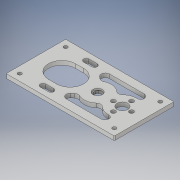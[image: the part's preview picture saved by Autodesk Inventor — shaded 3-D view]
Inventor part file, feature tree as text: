
AUTODESK INVENTOR PART (.ipt)
format: ipt  version: 2018 (Build 220112000, 112)  size: 195,584 bytes
history: native  units: in
note: dims shown in document units (in); Inventor stores cm internally (conversion verified against a paired STEP export)
features: extrude x1, sketch x1, fillet x1
ambient origin geometry x8: Origin, YZ Plane, XZ Plane, XY Plane, X Axis, Y Axis, Z Axis, Center Point
bodies: Solid1 (feature_tree)
feature tree (3):
  extrude  "Extrusion1"  Depth=0.1875in TaperAngle=0.0deg
  sketch  "Sketch1"  dims[d0=0.17in d1=0.1875in d2=0.0in]
  fillet  "Fillet3"  [1 undecoded]
note: 1 required parameter value undecoded (feature->parameter linkage not recoverable at this tier; creation-order binding heuristic only, values carry confidence <= 0.55)
